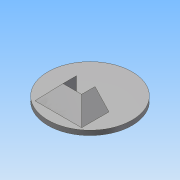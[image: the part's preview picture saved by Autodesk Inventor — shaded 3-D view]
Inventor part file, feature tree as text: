
AUTODESK INVENTOR PART (.ipt)
format: ipt  version: 2015 (Build 190159000, 159)  size: 116,224 bytes
history: native  units: mm
features: extrude x3, sketch x3, chamfer x2, plane x1, projected_geometry x1
ambient origin geometry x8: Origin, YZ Plane, XZ Plane, XY Plane, X Axis, Y Axis, Z Axis, Center Point
bodies: Volumenkörper1 (feature_tree)
feature tree (10):
  extrude  "Extrusion1"  Depth=1.0mm TaperAngle=0.0deg
  extrude  "Extrusion3"  Depth=2.875mm
  plane  "Arbeitsebene3"
  extrude  "Extrusion4"  Depth=3.3mm
  chamfer  "Fase1"  Distance=3.8mm
  chamfer  "Fase2"  Distance=3.3mm
  sketch  "Skizze1"  dims[d0=18.0mm d1=1.0mm d2=0.0mm]
  sketch  "Skizze2"  dims[d3=4.0mm d4=2.875mm]
  sketch  "Skizze5"  dims[d5=3.3mm d6=3.3mm d17=3.8mm d18=3.3mm d19=0.0mm d20=3.3mm d21=2.0mm d22=45.0deg d23=0.0mm d24=3.3mm d25=0.0mm d26=8.198926mm d27=3.3mm d28=8.198926mm d29=45.0deg]
  projected_geometry  "Projizierte Kontur1"
